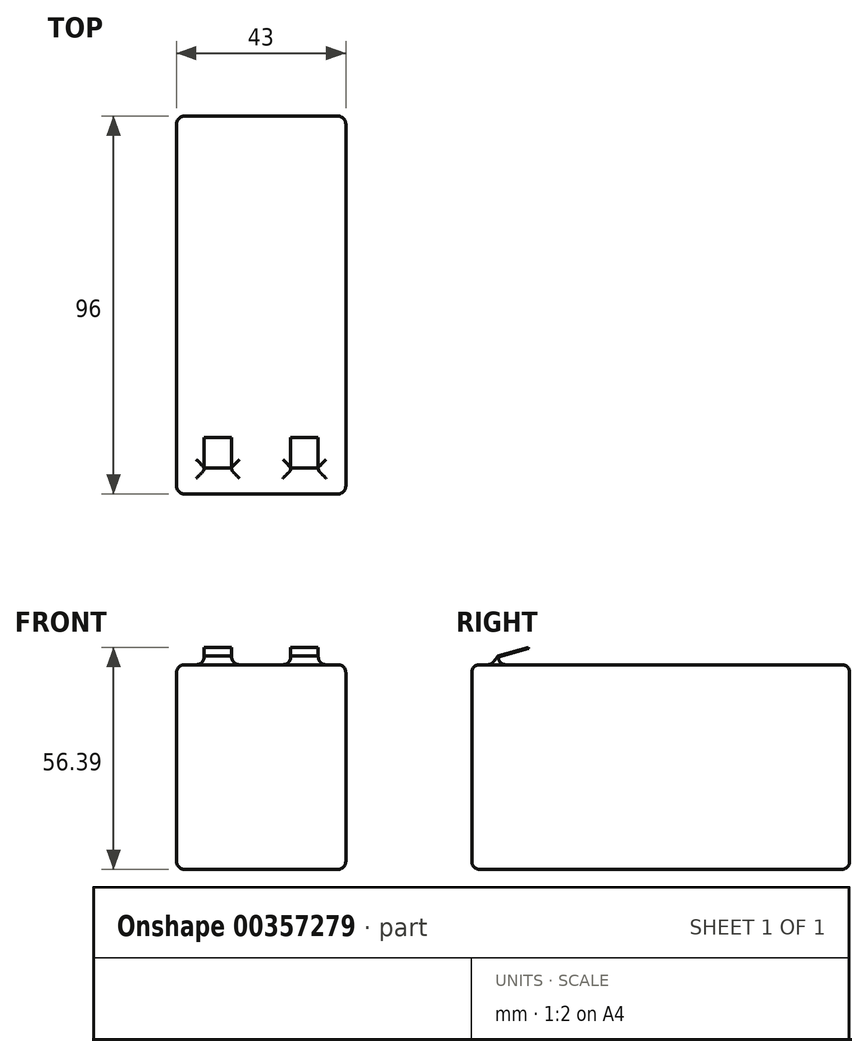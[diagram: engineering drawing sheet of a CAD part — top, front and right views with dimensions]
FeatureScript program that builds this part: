
annotation { "Feature Type Name" : "Feature", "Feature Type Description" : "" }
export const myFeature = defineFeature(function(context is Context, id is Id, definition is map)
    precondition{}
    {
        {
            var Q0;
            Q0=qCreatedBy(makeId("Top.planeOp"),FACE);
            var sketch = newSketch(context, id + "F0", { "sketchPlane" : qUnion([Q0])});
            skLineSegment(sketch, "E0.bottom", {"start": v(21.5, -48) * mm, "end": v(-21.5, -48) * mm});
            skLineSegment(sketch, "E0.top", {"start": v(21.5, 48) * mm, "end": v(-21.5, 48) * mm});
            skLineSegment(sketch, "E0.left", {"start": v(21.5, -48) * mm, "end": v(21.5, 48) * mm});
            skLineSegment(sketch, "E0.right", {"start": v(-21.5, -48) * mm, "end": v(-21.5, 48) * mm});
            skPoint(sketch, "E0.middle", {"position": v(0, 0) * mm});
            skSolve(sketch);
        }
        {
            var Q0;
            Q0=makeQuery(id+"F0.imprint","IMPRINT",FACE,{"disambiguationData":[TD([[makeQuery(id+"F0.imprint","IMPRINT",EDGE,{"derivedFrom":sQuery(id+"F0.wireOp",EDGE,"E0.bottom")}),-1.0]])]});
            extrude(context, id + "F1", {"entities" : qUnion([Q0]), "endBound" : BoundingType.SYMMETRIC, "depth" : 52 * mm});
        }
        {
            var Q0;
            Q0=qCreatedBy(makeId("Right.planeOp"),FACE);
            var sketch = newSketch(context, id + "F2", { "sketchPlane" : qUnion([Q0])});
            skLineSegment(sketch, "E1", {"start": v(-43.12, 25.92) * mm, "end": v(-41.35, 28.2) * mm});
            skLineSegment(sketch, "E2", {"start": v(-41.35, 28.2) * mm, "end": v(-33.65, 30.4) * mm});
            skLineSegment(sketch, "E3", {"start": v(-33.65, 30.4) * mm, "end": v(-33.6, 30.19) * mm});
            skLineSegment(sketch, "E4", {"start": v(-33.6, 30.19) * mm, "end": v(-41.27, 28) * mm});
            skLineSegment(sketch, "E5", {"start": v(-41.27, 28) * mm, "end": v(-42.89, 25.92) * mm});
            skLineSegment(sketch, "E6", {"start": v(-42.89, 25.92) * mm, "end": v(-43.12, 25.92) * mm});
            skSolve(sketch);
        }
        {
            var Q0;
            Q0 = qSketchRegion(id + "F2", true);
            extrude(context, id + "F3", {"entities" : qUnion([Q0]), "operationType" : NewBodyOperationType.ADD, "endBound" : BoundingType.SYMMETRIC, "depth" : 29 * mm});
        }
        {
            var Q0;
            Q0=makeQuery(id+"F1.opExtrude","SWEPT_FACE",FACE,{"disambiguationData":[OSD([sQuery(id+"F0.wireOp",EDGE,"E0.bottom")])]});
            var sketch = newSketch(context, id + "F4", { "sketchPlane" : qUnion([Q0])});
            skLineSegment(sketch, "E7.bottom", {"start": v(-7.5, 34.27) * mm, "end": v(7.5, 34.27) * mm});
            skLineSegment(sketch, "E7.top", {"start": v(-7.5, 26) * mm, "end": v(7.5, 26) * mm});
            skLineSegment(sketch, "E7.left", {"start": v(-7.5, 34.27) * mm, "end": v(-7.5, 26) * mm});
            skLineSegment(sketch, "E7.right", {"start": v(7.5, 34.27) * mm, "end": v(7.5, 26) * mm});
            skSolve(sketch);
        }
        {
            var Q0;
            Q0 = qSketchRegion(id + "F4", true);
            extrude(context, id + "F5", {"entities" : qUnion([Q0]), "operationType" : NewBodyOperationType.REMOVE, "oppositeDirection" : true, "depth" : 25 * mm});
        }
        {
            var Q0;
            Q0=makeQuery(id+"F1.opExtrude","SWEPT_FACE",FACE,{"disambiguationData":[OSD([sQuery(id+"F0.wireOp",EDGE,"E0.left")])]});
            var Q1;
            Q1=makeQuery(id+"F1.opExtrude","SWEPT_FACE",FACE,{"disambiguationData":[OSD([sQuery(id+"F0.wireOp",EDGE,"E0.bottom")])]});
            var Q2;
            Q2=makeQuery(id+"F1.opExtrude","SWEPT_FACE",FACE,{"disambiguationData":[OSD([sQuery(id+"F0.wireOp",EDGE,"E0.top")])]});
            var Q3;
            Q3=makeQuery(id+"F5.boolean.opBoolean","MERGE",FACE,{"derivedFrom":[makeQuery(id+"F1.opExtrude","CAP_FACE",FACE,{"disambiguationData":[OSD([sQuery(id+"F0.wireOp",EDGE,"E0.bottom"),sQuery(id+"F0.wireOp",EDGE,"E0.top"),sQuery(id+"F0.wireOp",EDGE,"E0.left"),sQuery(id+"F0.wireOp",EDGE,"E0.right")])],"isStart":false}),makeQuery(id+"F5.opExtrude","SWEPT_FACE",FACE,{"disambiguationData":[OSD([sQuery(id+"F4.wireOp",EDGE,"E7.top")])]})]});
            var Q4;
            Q4=makeQuery(id+"F1.opExtrude","SWEPT_FACE",FACE,{"disambiguationData":[OSD([sQuery(id+"F0.wireOp",EDGE,"E0.right")])]});
            var Q5;
            Q5=makeQuery(id+"F1.opExtrude","CAP_FACE",FACE,{"disambiguationData":[OSD([sQuery(id+"F0.wireOp",EDGE,"E0.bottom"),sQuery(id+"F0.wireOp",EDGE,"E0.top"),sQuery(id+"F0.wireOp",EDGE,"E0.left"),sQuery(id+"F0.wireOp",EDGE,"E0.right")])],"isStart":true});
            fillet(context, id + "F6", {"entities" : qUnion([Q0, Q1, Q2, Q3, Q4, Q5]), "radius" : 2 * mm, "allowEdgeOverflow" : false});
        }
    });
